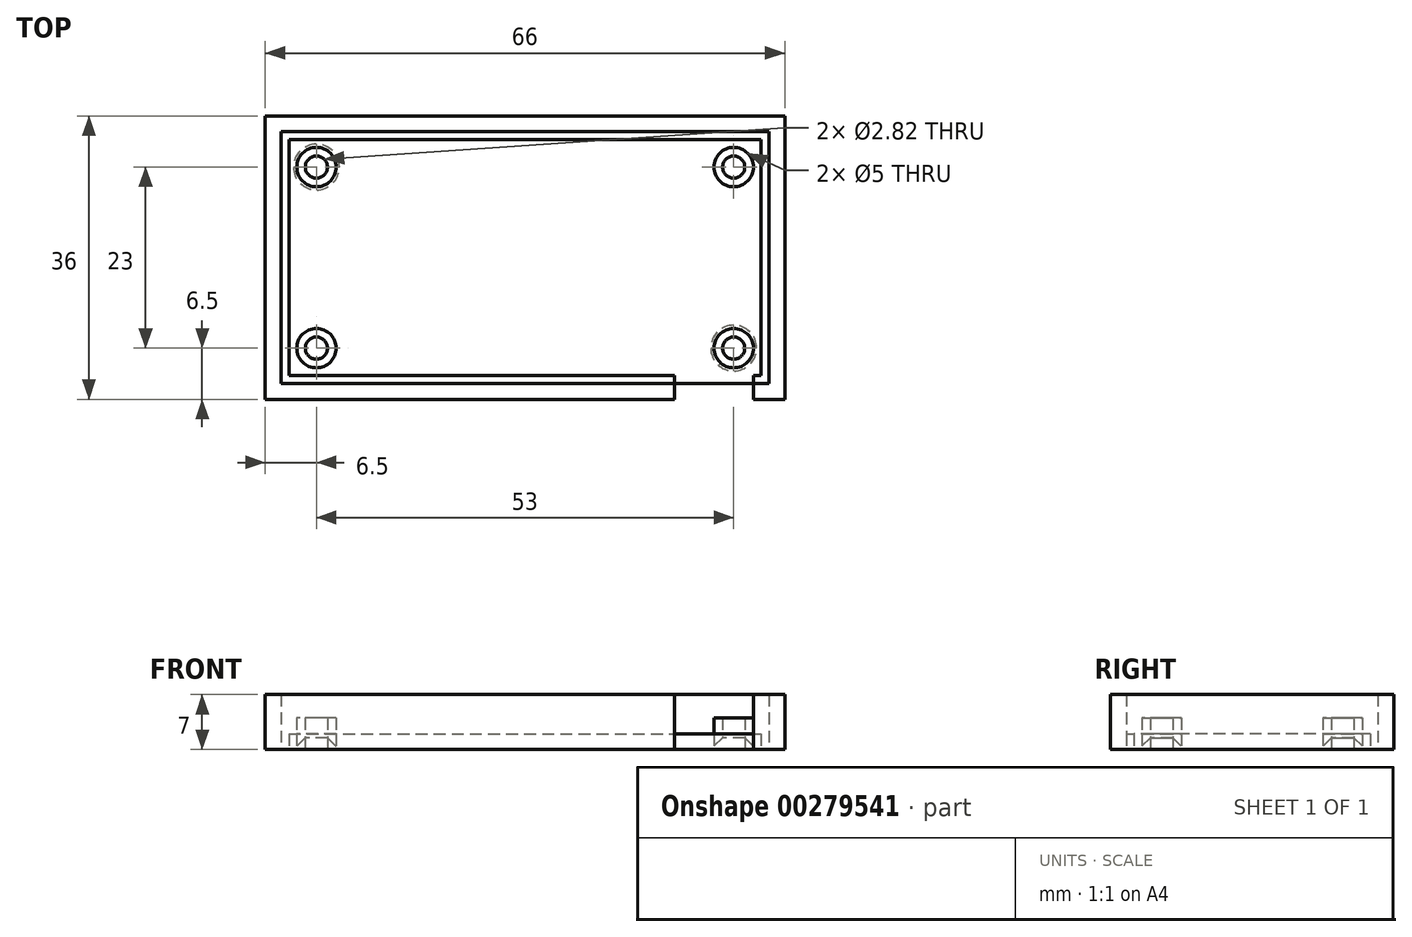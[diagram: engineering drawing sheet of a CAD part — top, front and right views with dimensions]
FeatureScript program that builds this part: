
annotation { "Feature Type Name" : "Feature", "Feature Type Description" : "" }
export const myFeature = defineFeature(function(context is Context, id is Id, definition is map)
    precondition{}
    {
        {
            var Q0;
            Q0=qCreatedBy(makeId("Top.planeOp"),FACE);
            var sketch = newSketch(context, id + "F0", { "sketchPlane" : qUnion([Q0])});
            skLineSegment(sketch, "E0.bottom", {"start": v(-30, 15) * mm, "end": v(30, 15) * mm});
            skLineSegment(sketch, "E0.top", {"start": v(-30, -15) * mm, "end": v(30, -15) * mm});
            skLineSegment(sketch, "E0.left", {"start": v(-30, 15) * mm, "end": v(-30, -15) * mm});
            skLineSegment(sketch, "E0.right", {"start": v(30, 15) * mm, "end": v(30, -15) * mm});
            skPoint(sketch, "E0.middle", {"position": v(0, 0) * mm});
            skCircle(sketch, "E1", {"center": v(-26.5, 11.5) * mm, "radius": 1.41 * mm});
            skLineSegment(sketch, "E2", {"start": v(-26.5, 15) * mm, "end": v(-26.5, 11.5) * mm});
            skCircle(sketch, "E3.MirrorC", {"center": v(26.5, 11.5) * mm, "radius": 1.41 * mm});
            skCircle(sketch, "E4.MirrorC", {"center": v(26.5, -11.5) * mm, "radius": 1.41 * mm});
            skCircle(sketch, "E5.MirrorC", {"center": v(-26.5, -11.5) * mm, "radius": 1.41 * mm});
            skLineSegment(sketch, "E6.0", {"start": v(-31, 16) * mm, "end": v(31, 16) * mm});
            skLineSegment(sketch, "E6.1", {"start": v(-31, 16) * mm, "end": v(-31, -16) * mm});
            skLineSegment(sketch, "E6.2", {"start": v(-31, -16) * mm, "end": v(31, -16) * mm});
            skLineSegment(sketch, "E6.3", {"start": v(31, 16) * mm, "end": v(31, -16) * mm});
            skLineSegment(sketch, "E7.0", {"start": v(-33, 18) * mm, "end": v(33, 18) * mm});
            skLineSegment(sketch, "E7.1", {"start": v(-33, 18) * mm, "end": v(-33, -18) * mm});
            skLineSegment(sketch, "E7.2", {"start": v(-33, -18) * mm, "end": v(33, -18) * mm});
            skLineSegment(sketch, "E7.3", {"start": v(33, 18) * mm, "end": v(33, -18) * mm});
            skLineSegment(sketch, "E8", {"start": v(-31, -16) * mm, "end": v(10.73, -16) * mm});
            skLineSegment(sketch, "E9", {"start": v(-30, -15) * mm, "end": v(24, -15) * mm});
            skLineSegment(sketch, "E10.bottom", {"start": v(29, -18) * mm, "end": v(19, -18) * mm});
            skLineSegment(sketch, "E10.top", {"start": v(29, -15) * mm, "end": v(19, -15) * mm});
            skLineSegment(sketch, "E10.left", {"start": v(29, -18) * mm, "end": v(29, -15) * mm});
            skLineSegment(sketch, "E10.right", {"start": v(19, -18) * mm, "end": v(19, -15) * mm});
            skPoint(sketch, "E10.middle", {"position": v(24, -16.5) * mm});
            skCircle(sketch, "E11", {"center": v(26.5, 11.5) * mm, "radius": 2.5 * mm});
            skCircle(sketch, "E12.MirrorC", {"center": v(-26.5, 11.5) * mm, "radius": 2.5 * mm});
            skCircle(sketch, "E13.MirrorC", {"center": v(-26.5, -11.5) * mm, "radius": 2.5 * mm});
            skCircle(sketch, "E14.MirrorC", {"center": v(26.5, -11.5) * mm, "radius": 2.5 * mm});
            skSolve(sketch);
        }
        {
            var Q0;
            Q0=makeQuery(id+"F0.imprint","IMPRINT",FACE,{"disambiguationData":[TD([[makeQuery(id+"F0.imprint","IMPRINT",EDGE,{"derivedFrom":sQuery(id+"F0.wireOp",EDGE,"E6.0")}),1.0]])]});
            var Q1;
            {var subQ12=sQuery(id+"F0.wireOp",EDGE,"E0.top");Q1=makeQuery(id+"F0.imprint","IMPRINT",FACE,{"disambiguationData":[TD([[makeQuery(id+"F0.imprint","IMPRINT",EDGE,{"derivedFrom":subQ12}),-1.0]])]});}
            var Q2;
            {var subQ7=sQuery(id+"F0.wireOp",EDGE,"E0.top");Q2=makeQuery(id+"F0.imprint","IMPRINT",FACE,{"disambiguationData":[TD([[makeQuery(id+"F0.imprint","IMPRINT",EDGE,{"derivedFrom":subQ7}),1.0]])]});}
            var Q3;
            Q3=makeQuery(id+"F0.imprint","IMPRINT",FACE,{"disambiguationData":[TD([[makeQuery(id+"F0.imprint","IMPRINT",EDGE,{"derivedFrom":sQuery(id+"F0.wireOp",EDGE,"E1")}),-1.0]])]});
            var Q4;
            Q4=makeQuery(id+"F0.imprint","IMPRINT",FACE,{"disambiguationData":[TD([[makeQuery(id+"F0.imprint","IMPRINT",EDGE,{"derivedFrom":sQuery(id+"F0.wireOp",EDGE,"E5.MirrorC")}),1.0]])]});
            var Q5;
            Q5=makeQuery(id+"F0.imprint","IMPRINT",FACE,{"disambiguationData":[TD([[makeQuery(id+"F0.imprint","IMPRINT",EDGE,{"derivedFrom":sQuery(id+"F0.wireOp",EDGE,"E4.MirrorC")}),-1.0]])]});
            var Q6;
            Q6=makeQuery(id+"F0.imprint","IMPRINT",FACE,{"disambiguationData":[TD([[makeQuery(id+"F0.imprint","IMPRINT",EDGE,{"derivedFrom":sQuery(id+"F0.wireOp",EDGE,"E3.MirrorC")}),1.0]])]});
            var Q7;
            {var subQ3=sQuery(id+"F0.wireOp",EDGE,"E6.2");var subQ5=sQuery(id+"F0.wireOp",EDGE,"E10.right");var subQ8=makeQuery(id+"F0.imprint","INTERSECT",VERTEX,{"derivedFrom":[subQ3,subQ5]});Q7=makeQuery(id+"F0.imprint","IMPRINT",FACE,{"disambiguationData":[TD([[makeQuery(id+"F0.imprint","IMPRINT",EDGE,{"disambiguationData":[TD([[subQ8,-1.0]])],"derivedFrom":subQ3}),1.0]])]});}
            var Q8;
            {var subQ5=sQuery(id+"F0.wireOp",EDGE,"E10.bottom");Q8=makeQuery(id+"F0.imprint","IMPRINT",FACE,{"disambiguationData":[TD([[makeQuery(id+"F0.imprint","IMPRINT",EDGE,{"derivedFrom":subQ5}),-1.0]])]});}
            extrude(context, id + "F1", {"entities" : qUnion([Q0, Q1, Q2, Q3, Q4, Q5, Q6, Q7, Q8]), "depth" : 2 * mm});
        }
        {
            var Q0;
            Q0=makeQuery(id+"F0.imprint","IMPRINT",FACE,{"disambiguationData":[TD([[makeQuery(id+"F0.imprint","IMPRINT",EDGE,{"derivedFrom":sQuery(id+"F0.wireOp",EDGE,"E5.MirrorC")}),1.0]])]});
            var Q1;
            Q1=makeQuery(id+"F0.imprint","IMPRINT",FACE,{"disambiguationData":[TD([[makeQuery(id+"F0.imprint","IMPRINT",EDGE,{"derivedFrom":sQuery(id+"F0.wireOp",EDGE,"E1")}),-1.0]])]});
            var Q2;
            Q2=makeQuery(id+"F0.imprint","IMPRINT",FACE,{"disambiguationData":[TD([[makeQuery(id+"F0.imprint","IMPRINT",EDGE,{"derivedFrom":sQuery(id+"F0.wireOp",EDGE,"E4.MirrorC")}),-1.0]])]});
            var Q3;
            Q3=makeQuery(id+"F0.imprint","IMPRINT",FACE,{"disambiguationData":[TD([[makeQuery(id+"F0.imprint","IMPRINT",EDGE,{"derivedFrom":sQuery(id+"F0.wireOp",EDGE,"E3.MirrorC")}),1.0]])]});
            extrude(context, id + "F2", {"entities" : qUnion([Q0, Q1, Q2, Q3]), "operationType" : NewBodyOperationType.ADD, "depth" : 4 * mm});
        }
        {
            var Q0;
            Q0=makeQuery(id+"F0.imprint","IMPRINT",FACE,{"disambiguationData":[TD([[makeQuery(id+"F0.imprint","IMPRINT",EDGE,{"derivedFrom":sQuery(id+"F0.wireOp",EDGE,"E6.0")}),1.0]])]});
            extrude(context, id + "F3", {"entities" : qUnion([Q0]), "operationType" : NewBodyOperationType.ADD, "depth" : 7 * mm});
        }
        {
            var Q0;
            Q0=makeQuery(id+"F1.opExtrude","CAP_EDGE",EDGE,{"disambiguationData":[OSD([sQuery(id+"F0.wireOp",EDGE,"E4.MirrorC")])],"isStart":true});
            var Q1;
            Q1=makeQuery(id+"F1.opExtrude","CAP_EDGE",EDGE,{"disambiguationData":[OSD([sQuery(id+"F0.wireOp",EDGE,"E3.MirrorC")])],"isStart":true});
            var Q2;
            Q2=makeQuery(id+"F1.opExtrude","CAP_EDGE",EDGE,{"disambiguationData":[OSD([sQuery(id+"F0.wireOp",EDGE,"E1")])],"isStart":true});
            var Q3;
            Q3=makeQuery(id+"F1.opExtrude","CAP_EDGE",EDGE,{"disambiguationData":[OSD([sQuery(id+"F0.wireOp",EDGE,"E5.MirrorC")])],"isStart":true});
            chamfer(context, id + "F4", {"entities" : qUnion([Q0, Q1, Q2, Q3]), "width" : 1.5 * mm, "tangentPropagation" : true});
        }
    });
